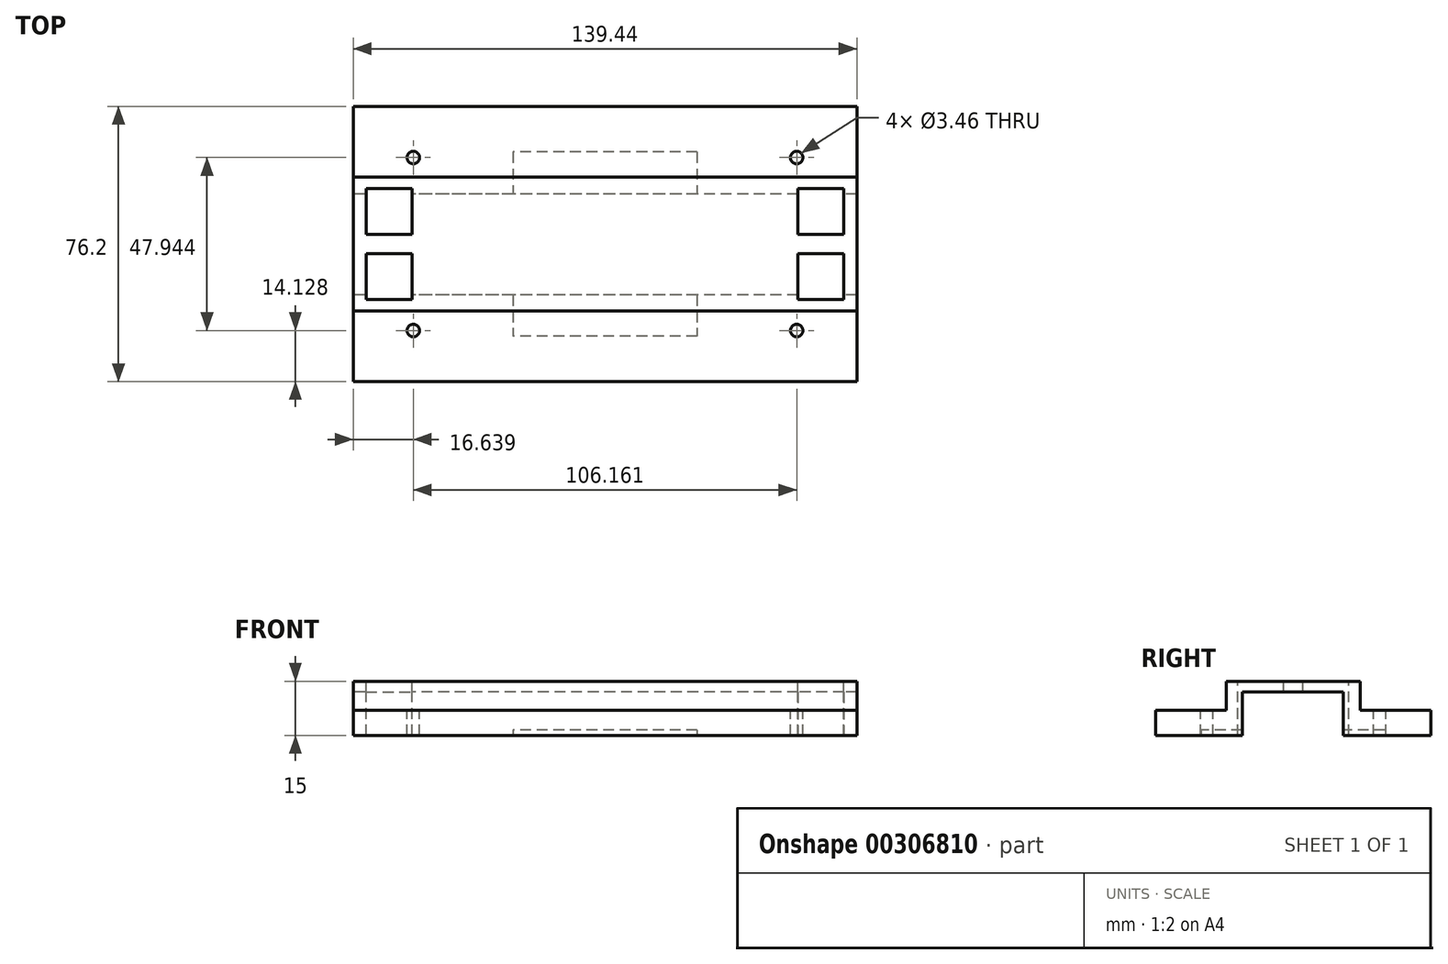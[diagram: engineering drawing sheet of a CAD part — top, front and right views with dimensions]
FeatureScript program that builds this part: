
annotation { "Feature Type Name" : "Feature", "Feature Type Description" : "" }
export const myFeature = defineFeature(function(context is Context, id is Id, definition is map)
    precondition{}
    {
        {
            var Q0;
            Q0=qCreatedBy(makeId("Front.planeOp"),FACE);
            var sketch = newSketch(context, id + "F0", { "sketchPlane" : qUnion([Q0])});
            skLineSegment(sketch, "E0.bottom", {"start": v(69.72, 7.5) * mm, "end": v(-69.72, 7.5) * mm});
            skLineSegment(sketch, "E0.top", {"start": v(69.72, -7.5) * mm, "end": v(-69.72, -7.5) * mm});
            skLineSegment(sketch, "E0.left", {"start": v(69.72, 7.5) * mm, "end": v(69.72, -7.5) * mm});
            skLineSegment(sketch, "E0.right", {"start": v(-69.72, 7.5) * mm, "end": v(-69.72, -7.5) * mm});
            skPoint(sketch, "E0.middle", {"position": v(0, 0) * mm});
            skSolve(sketch);
        }
        {
            var Q0;
            Q0 = qSketchRegion(id + "F0", true);
            extrude(context, id + "F1", {"entities" : qUnion([Q0]), "endBound" : BoundingType.SYMMETRIC, "depth" : 76.2 * mm});
        }
        {
            var Q0;
            Q0=makeQuery(id+"F1.opExtrude","SWEPT_FACE",FACE,{"disambiguationData":[OSD([sQuery(id+"F0.wireOp",EDGE,"E0.bottom")])]});
            var sketch = newSketch(context, id + "F2", { "sketchPlane" : qUnion([Q0])});
            skLineSegment(sketch, "E1.bottom", {"start": v(-69.72, -38.1) * mm, "end": v(69.72, -38.1) * mm});
            skLineSegment(sketch, "E1.top", {"start": v(-69.72, -18.53) * mm, "end": v(69.72, -18.53) * mm});
            skLineSegment(sketch, "E1.left", {"start": v(-69.72, -38.1) * mm, "end": v(-69.72, -18.53) * mm});
            skLineSegment(sketch, "E1.right", {"start": v(69.72, -38.1) * mm, "end": v(69.72, -18.53) * mm});
            skSolve(sketch);
        }
        {
            var Q0;
            Q0=makeQuery(id+"F2.imprint","IMPRINT",FACE,{"disambiguationData":[TD([[makeQuery(id+"F2.imprint","IMPRINT",EDGE,{"derivedFrom":sQuery(id+"F2.wireOp",EDGE,"E1.bottom")}),-1.0]])]});
            extrude(context, id + "F3", {"entities" : qUnion([Q0]), "operationType" : NewBodyOperationType.REMOVE, "oppositeDirection" : true, "depth" : 8 * mm});
        }
        {
            var Q0;
            Q0=makeQuery(id+"F1.opExtrude","SWEPT_BODY",BODY,{"disambiguationData":[OSD([sQuery(id+"F0.wireOp",EDGE,"E0.bottom"),sQuery(id+"F0.wireOp",EDGE,"E0.top"),sQuery(id+"F0.wireOp",EDGE,"E0.left"),sQuery(id+"F0.wireOp",EDGE,"E0.right")])]});
            var Q1;
            Q1=qCreatedBy(makeId("Front.planeOp"),FACE);
            mirror(context, id + "F4", {"operationType" : NewBodyOperationType.INTERSECT, "entities" : qUnion([Q0]), "mirrorPlane" : qUnion([Q1])});
        }
        {
            var Q0;
            Q0=makeQuery(id+"F1.opExtrude","SWEPT_FACE",FACE,{"disambiguationData":[OSD([sQuery(id+"F0.wireOp",EDGE,"E0.bottom")])]});
            var sketch = newSketch(context, id + "F5", { "sketchPlane" : qUnion([Q0])});
            skLineSegment(sketch, "E2.bottom", {"start": v(66.14, -15.37) * mm, "end": v(53.44, -15.37) * mm});
            skLineSegment(sketch, "E2.top", {"start": v(66.14, -2.67) * mm, "end": v(53.44, -2.67) * mm});
            skLineSegment(sketch, "E2.left", {"start": v(66.14, -15.37) * mm, "end": v(66.14, -2.67) * mm});
            skLineSegment(sketch, "E2.right", {"start": v(53.44, -15.37) * mm, "end": v(53.44, -2.67) * mm});
            skSolve(sketch);
        }
        {
            var Q0;
            Q0=makeQuery(id+"F5.imprint","IMPRINT",FACE,{"disambiguationData":[TD([[makeQuery(id+"F5.imprint","IMPRINT",EDGE,{"derivedFrom":sQuery(id+"F5.wireOp",EDGE,"E2.bottom")}),-1.0]])]});
            extrude(context, id + "F6", {"entities" : qUnion([Q0]), "operationType" : NewBodyOperationType.REMOVE, "oppositeDirection" : true, "depth" : 21.84 * mm});
        }
        {
            var Q0;
            Q0=makeQuery(id+"F1.opExtrude","SWEPT_BODY",BODY,{"disambiguationData":[OSD([sQuery(id+"F0.wireOp",EDGE,"E0.bottom"),sQuery(id+"F0.wireOp",EDGE,"E0.top"),sQuery(id+"F0.wireOp",EDGE,"E0.left"),sQuery(id+"F0.wireOp",EDGE,"E0.right")])]});
            var Q1;
            Q1=qCreatedBy(makeId("Front.planeOp"),FACE);
            mirror(context, id + "F7", {"operationType" : NewBodyOperationType.INTERSECT, "entities" : qUnion([Q0]), "mirrorPlane" : qUnion([Q1])});
        }
        {
            var Q0;
            Q0=makeQuery(id+"F1.opExtrude","SWEPT_BODY",BODY,{"disambiguationData":[OSD([sQuery(id+"F0.wireOp",EDGE,"E0.bottom"),sQuery(id+"F0.wireOp",EDGE,"E0.top"),sQuery(id+"F0.wireOp",EDGE,"E0.left"),sQuery(id+"F0.wireOp",EDGE,"E0.right")])]});
            var Q1;
            Q1=qCreatedBy(makeId("Right.planeOp"),FACE);
            mirror(context, id + "F8", {"operationType" : NewBodyOperationType.INTERSECT, "entities" : qUnion([Q0]), "mirrorPlane" : qUnion([Q1])});
        }
        {
            var Q0;
            Q0=qCreatedBy(makeId("Top.planeOp"),FACE);
            var sketch = newSketch(context, id + "F9", { "sketchPlane" : qUnion([Q0])});
            skPoint(sketch, "E3.middle", {"position": v(0, 0) * mm});
            skCircle(sketch, "E4", {"center": v(53.08, -23.97) * mm, "radius": 1.73 * mm});
            skCircle(sketch, "E5", {"center": v(53.08, 23.97) * mm, "radius": 1.73 * mm});
            skCircle(sketch, "E6", {"center": v(-53.08, 23.97) * mm, "radius": 1.73 * mm});
            skCircle(sketch, "E7", {"center": v(-53.08, -23.97) * mm, "radius": 1.73 * mm});
            skSolve(sketch);
        }
        {
            var Q0;
            Q0=makeQuery(id+"F9.imprint","IMPRINT",FACE,{"disambiguationData":[TD([[makeQuery(id+"F9.imprint","IMPRINT",EDGE,{"derivedFrom":sQuery(id+"F9.wireOp",EDGE,"E4")}),1.0]])]});
            var Q1;
            Q1=makeQuery(id+"F9.imprint","IMPRINT",FACE,{"disambiguationData":[TD([[makeQuery(id+"F9.imprint","IMPRINT",EDGE,{"derivedFrom":sQuery(id+"F9.wireOp",EDGE,"E5")}),1.0]])]});
            var Q2;
            Q2=makeQuery(id+"F9.imprint","IMPRINT",FACE,{"disambiguationData":[TD([[makeQuery(id+"F9.imprint","IMPRINT",EDGE,{"derivedFrom":sQuery(id+"F9.wireOp",EDGE,"E6")}),1.0]])]});
            var Q3;
            Q3=makeQuery(id+"F9.imprint","IMPRINT",FACE,{"disambiguationData":[TD([[makeQuery(id+"F9.imprint","IMPRINT",EDGE,{"derivedFrom":sQuery(id+"F9.wireOp",EDGE,"E7")}),1.0]])]});
            extrude(context, id + "F10", {"entities" : qUnion([Q0, Q1, Q2, Q3]), "operationType" : NewBodyOperationType.REMOVE, "oppositeDirection" : true, "depth" : 42.16 * mm});
        }
        {
            var Q0;
            Q0=makeQuery(id+"F1.opExtrude","SWEPT_FACE",FACE,{"disambiguationData":[OSD([sQuery(id+"F0.wireOp",EDGE,"E0.top")])]});
            var sketch = newSketch(context, id + "F11", { "sketchPlane" : qUnion([Q0])});
            skPoint(sketch, "E8", {"position": v(35.36, 4.1) * mm});
            skLineSegment(sketch, "E9.bottom", {"start": v(69.72, 14.1) * mm, "end": v(1.72, 14.1) * mm});
            skLineSegment(sketch, "E9.top", {"start": v(69.72, -13.9) * mm, "end": v(1.72, -13.9) * mm});
            skLineSegment(sketch, "E9.left", {"start": v(69.72, 14.1) * mm, "end": v(69.72, -13.9) * mm});
            skLineSegment(sketch, "E10", {"start": v(1.72, 14.1) * mm, "end": v(-69.72, 14.1) * mm});
            skLineSegment(sketch, "E11", {"start": v(1.72, -13.9) * mm, "end": v(-69.72, -13.9) * mm});
            skLineSegment(sketch, "E12", {"start": v(-69.72, -13.9) * mm, "end": v(-69.72, 14.1) * mm});
            skPoint(sketch, "E13.oppositeSnap0", {"position": v(59.8, 15.37) * mm});
            skPoint(sketch, "E14.oppositeSnap0", {"position": v(59.8, -15.37) * mm});
            skPoint(sketch, "E15.oppositeSnap0", {"position": v(-59.8, -15.37) * mm});
            skPoint(sketch, "E16.oppositeSnap0", {"position": v(-59.8, 15.37) * mm});
            skSolve(sketch);
        }
        {
            var Q0;
            Q0=makeQuery(id+"F1.opExtrude","SWEPT_FACE",FACE,{"disambiguationData":[OSD([sQuery(id+"F0.wireOp",EDGE,"E0.top")])]});
            var sketch = newSketch(context, id + "F12", { "sketchPlane" : qUnion([Q0])});
            skLineSegment(sketch, "E17.bottom", {"start": v(25.5, -25.5) * mm, "end": v(-25.5, -25.5) * mm});
            skLineSegment(sketch, "E17.top", {"start": v(25.5, 25.5) * mm, "end": v(-25.5, 25.5) * mm});
            skLineSegment(sketch, "E17.left", {"start": v(25.5, -25.5) * mm, "end": v(25.5, 25.5) * mm});
            skLineSegment(sketch, "E17.right", {"start": v(-25.5, -25.5) * mm, "end": v(-25.5, 25.5) * mm});
            skPoint(sketch, "E17.middle", {"position": v(0, 0) * mm});
            skSolve(sketch);
        }
        {
            var Q0;
            Q0 = qSketchRegion(id + "F12", true);
            extrude(context, id + "F13", {"entities" : qUnion([Q0]), "operationType" : NewBodyOperationType.REMOVE, "oppositeDirection" : true, "depth" : 1.5 * mm});
        }
        {
            var Q0;
            Q0 = qSketchRegion(id + "F11", true);
            extrude(context, id + "F14", {"entities" : qUnion([Q0]), "operationType" : NewBodyOperationType.REMOVE, "oppositeDirection" : true, "depth" : 12 * mm});
        }
    });
